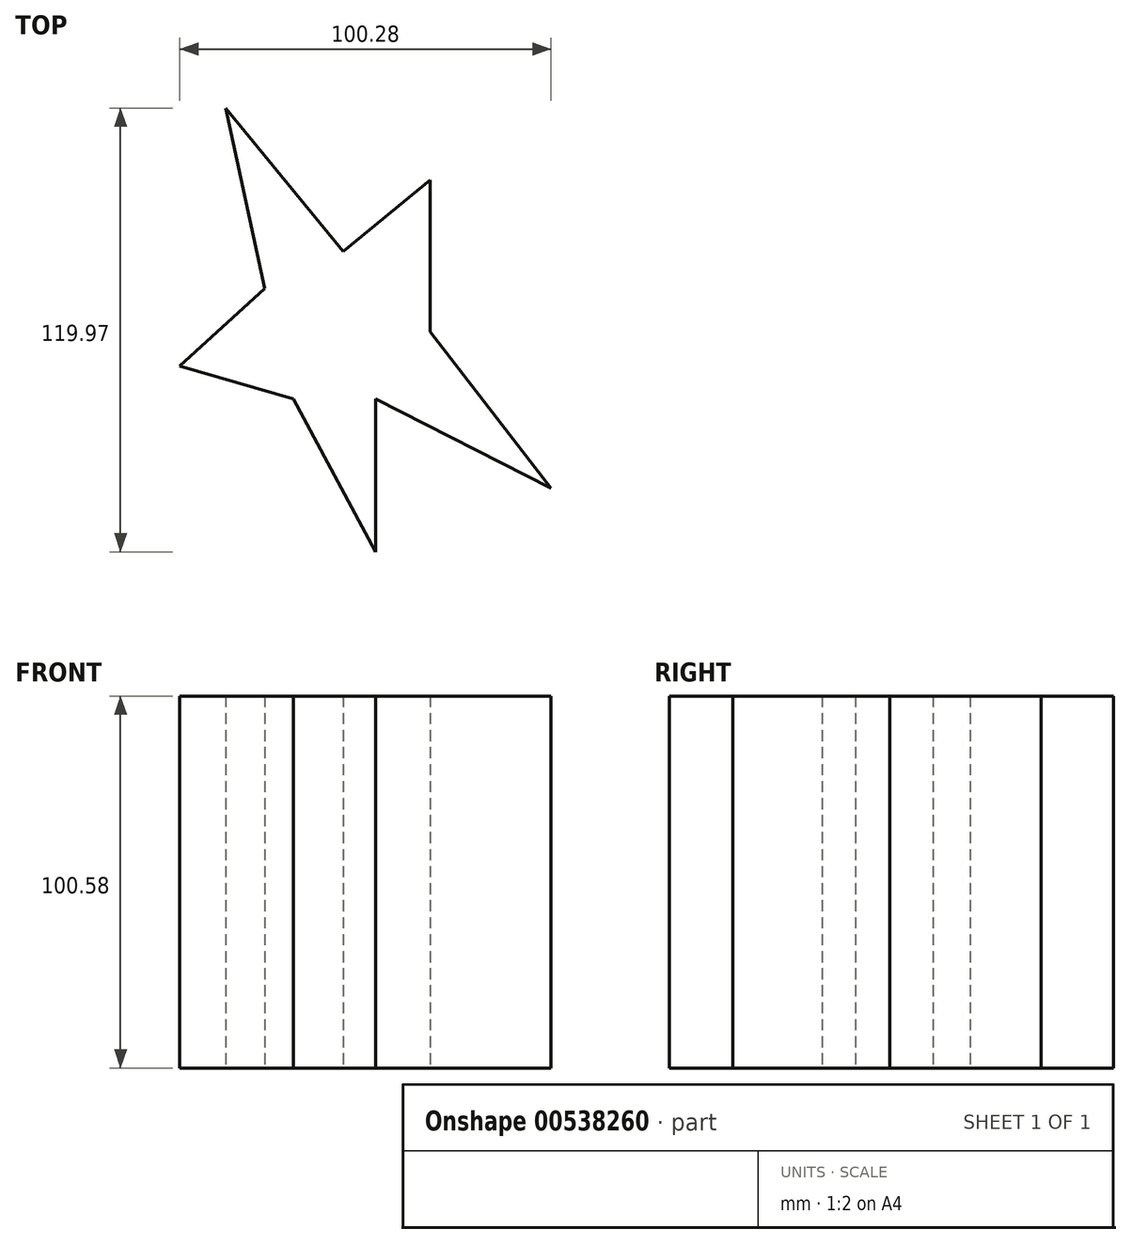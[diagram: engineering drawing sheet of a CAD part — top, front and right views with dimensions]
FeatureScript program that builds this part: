
annotation { "Feature Type Name" : "Feature", "Feature Type Description" : "" }
export const myFeature = defineFeature(function(context is Context, id is Id, definition is map)
    precondition{}
    {
        {
            var Q0;
            Q0=qCreatedBy(makeId("Top.planeOp"),FACE);
            var sketch = newSketch(context, id + "F0", { "sketchPlane" : qUnion([Q0])});
            skLineSegment(sketch, "E0", {"start": v(-90.86, -148.17) * mm, "end": v(-101.44, -99.45) * mm});
            skLineSegment(sketch, "E1", {"start": v(-101.44, -99.45) * mm, "end": v(-69.76, -138.19) * mm});
            skLineSegment(sketch, "E2", {"start": v(-69.76, -138.19) * mm, "end": v(-46.18, -118.9) * mm});
            skLineSegment(sketch, "E3", {"start": v(-46.18, -118.9) * mm, "end": v(-46.18, -159.88) * mm});
            skLineSegment(sketch, "E4", {"start": v(-46.18, -159.88) * mm, "end": v(-13.57, -202.26) * mm});
            skLineSegment(sketch, "E5", {"start": v(-13.57, -202.26) * mm, "end": v(-60.98, -178.08) * mm});
            skLineSegment(sketch, "E6", {"start": v(-60.98, -178.08) * mm, "end": v(-60.98, -219.42) * mm});
            skLineSegment(sketch, "E7", {"start": v(-60.98, -219.42) * mm, "end": v(-83.2, -178.08) * mm});
            skLineSegment(sketch, "E8", {"start": v(-83.2, -178.08) * mm, "end": v(-113.85, -169.13) * mm});
            skLineSegment(sketch, "E9", {"start": v(-113.85, -169.13) * mm, "end": v(-90.86, -148.17) * mm});
            skSolve(sketch);
        }
        {
            var Q0;
            Q0 = qSketchRegion(id + "F0", true);
            extrude(context, id + "F1", {"entities" : qUnion([Q0]), "depth" : 100.58 * mm, "offsetDistance" : 25.4 * mm});
        }
    });
